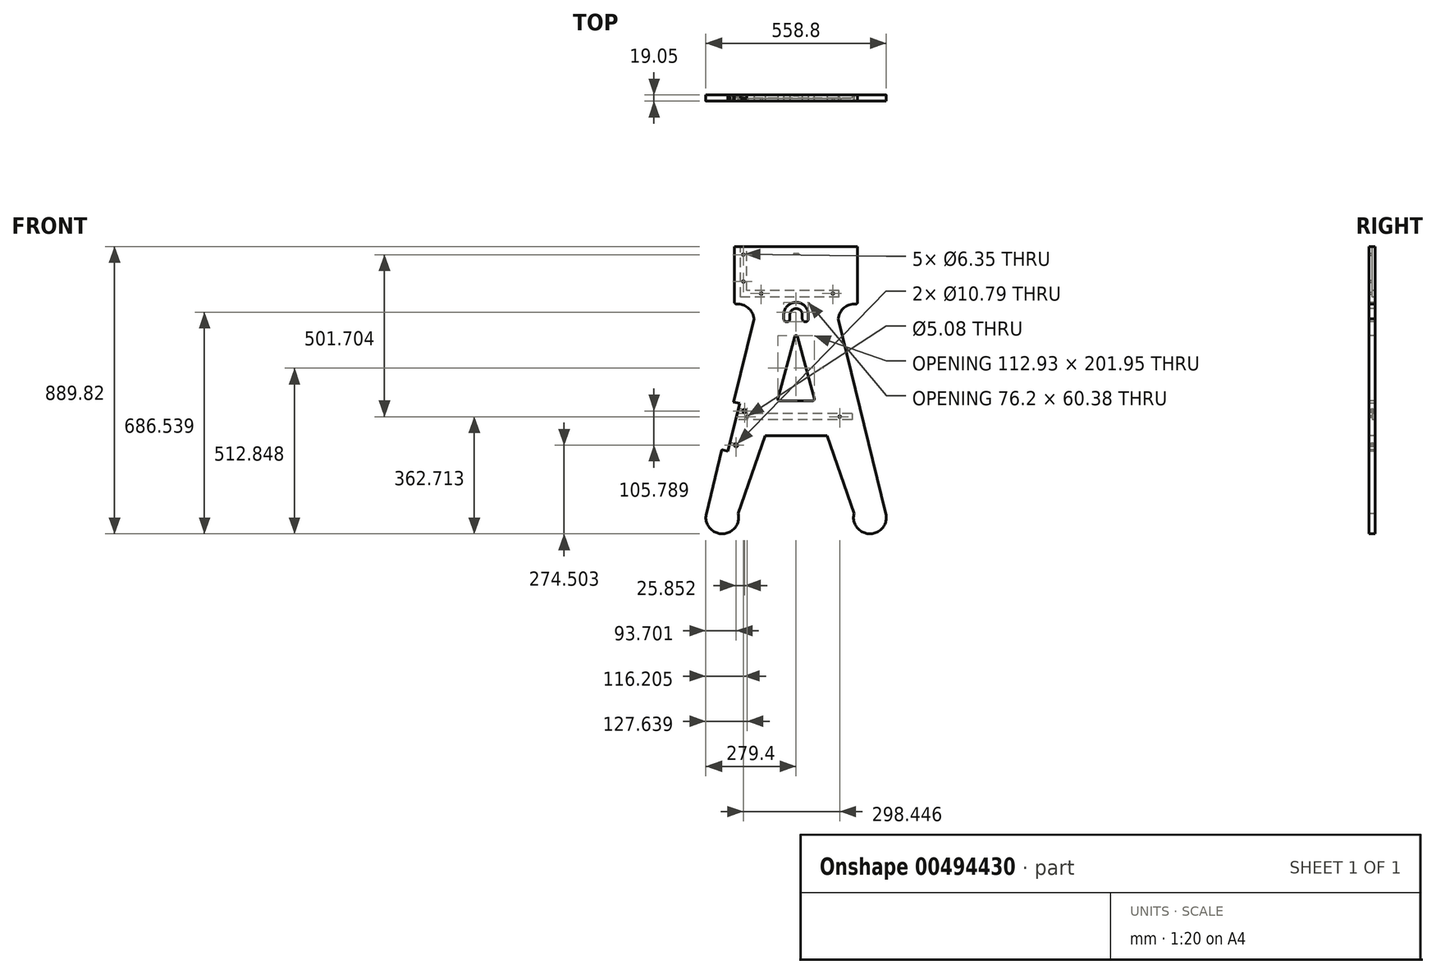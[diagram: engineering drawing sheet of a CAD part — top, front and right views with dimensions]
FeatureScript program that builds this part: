
annotation { "Feature Type Name" : "Feature", "Feature Type Description" : "" }
export const myFeature = defineFeature(function(context is Context, id is Id, definition is map)
    precondition{}
    {
        {
            var Q0;
            Q0=qCreatedBy(makeId("Front.planeOp"),FACE);
            var sketch = newSketch(context, id + "F0", { "sketchPlane" : qUnion([Q0])});
            skLineSegment(sketch, "E0", {"start": v(-190.5, 125.54) * mm, "end": v(-190.5, -53.23) * mm});
            skLineSegment(sketch, "E1", {"start": v(-173.35, -392.04) * mm, "end": v(-173.35, -411.49) * mm});
            skPoint(sketch, "E2.visualSharp", {"position": v(-190.5, -52.26) * mm});
            skLineSegment(sketch, "E3", {"start": v(-152.4, -30.85) * mm, "end": v(-152.4, -11.4) * mm});
            skLineSegment(sketch, "E4", {"start": v(0, -85.65) * mm, "end": v(0, -6.48) * mm, "construction": true});
            skLineSegment(sketch, "E5", {"start": v(-130.6, -98.45) * mm, "end": v(-277.95, -701.42) * mm});
            skArc(sketch, "E6", {"start": v(-277.95, -701.42) * mm, "mid": v(-228.6, -764.28) * mm, "end": v(-179.25, -701.42) * mm});
            skLineSegment(sketch, "E7", {"start": v(0, 125.54) * mm, "end": v(0, -789) * mm, "construction": true});
            skPoint(sketch, "E8", {"position": v(-95.55, -460.12) * mm});
            skPoint(sketch, "E9", {"position": v(0, -135.91) * mm});
            skPoint(sketch, "E10", {"position": v(-58, -352.4) * mm});
            skLineSegment(sketch, "E11", {"start": v(0, -400.38) * mm, "end": v(0, -411.49) * mm});
            skLineSegment(sketch, "E12", {"start": v(-179.25, -701.42) * mm, "end": v(-95.55, -460.12) * mm});
            skLineSegment(sketch, "E13", {"start": v(95.55, -460.12) * mm, "end": v(-95.55, -460.12) * mm});
            skLineSegment(sketch, "E14", {"start": v(0, -135.91) * mm, "end": v(-58, -352.4) * mm});
            skLineSegment(sketch, "E15", {"start": v(-200.12, -382.94) * mm, "end": v(-236.3, -530.98) * mm});
            skLineSegment(sketch, "E16", {"start": v(-193.57, -356.14) * mm, "end": v(-175.06, -360.66) * mm});
            skLineSegment(sketch, "E17", {"start": v(-175.06, -360.66) * mm, "end": v(-211.24, -508.7) * mm});
            skLineSegment(sketch, "E18", {"start": v(-211.24, -508.7) * mm, "end": v(-229.75, -504.18) * mm});
            skPoint(sketch, "E19", {"position": v(-228.6, -764.28) * mm});
            skLineSegment(sketch, "E20", {"start": v(-228.6, -764.28) * mm, "end": v(190.5, -764.28) * mm, "construction": true});
            skLineSegment(sketch, "E21.MirrorCS", {"start": v(-171.45, 124.72) * mm, "end": v(-209.55, 124.72) * mm, "construction": true});
            skLineSegment(sketch, "E22", {"start": v(-190.5, 125.54) * mm, "end": v(-228.6, 125.54) * mm, "construction": true});
            skPoint(sketch, "E23", {"position": v(-173.35, -392.04) * mm});
            skPoint(sketch, "E24", {"position": v(-173.35, -411.49) * mm});
            skLineSegment(sketch, "E25", {"start": v(-173.35, -392.04) * mm, "end": v(173.35, -392.04) * mm});
            skLineSegment(sketch, "E26", {"start": v(173.35, -411.49) * mm, "end": v(-173.35, -411.49) * mm});
            skLineSegment(sketch, "E27", {"start": v(-228.6, 125.54) * mm, "end": v(-228.6, -764.28) * mm, "construction": true});
            skPoint(sketch, "E28", {"position": v(0, 125.54) * mm});
            skPoint(sketch, "E29", {"position": v(0, -11.4) * mm});
            skPoint(sketch, "E30", {"position": v(0, -30.85) * mm});
            skPoint(sketch, "E31", {"position": v(0, -66.6) * mm});
            skPoint(sketch, "E32", {"position": v(0, -46.07) * mm});
            skPoint(sketch, "E33", {"position": v(0, -104.7) * mm});
            skPoint(sketch, "E34", {"position": v(0, -352.4) * mm});
            skPoint(sketch, "E35", {"position": v(0, -460.12) * mm});
            skPoint(sketch, "E36", {"position": v(-19.05, -701.42) * mm});
            skLineSegment(sketch, "E37", {"start": v(0, -460.12) * mm, "end": v(95.55, -460.12) * mm});
            skLineSegment(sketch, "E38", {"start": v(0, -411.49) * mm, "end": v(173.35, -411.49) * mm});
            skLineSegment(sketch, "E39", {"start": v(173.35, -392.04) * mm, "end": v(0, -392.04) * mm});
            skLineSegment(sketch, "E40", {"start": v(-179.25, -701.42) * mm, "end": v(-19.05, -701.42) * mm});
            skLineSegment(sketch, "E41", {"start": v(0, 125.54) * mm, "end": v(-190.5, 125.54) * mm});
            skLineSegment(sketch, "E42", {"start": v(0, -11.4) * mm, "end": v(-152.4, -11.4) * mm});
            skLineSegment(sketch, "E43", {"start": v(-152.4, -30.85) * mm, "end": v(0, -30.85) * mm});
            skLineSegment(sketch, "E44", {"start": v(-58, -352.4) * mm, "end": v(0, -352.4) * mm});
            skLineSegment(sketch, "E45.MirrorCS", {"start": v(0, 125.54) * mm, "end": v(190.5, 125.54) * mm});
            skLineSegment(sketch, "E46.MirrorCS", {"start": v(190.5, 125.54) * mm, "end": v(190.5, -53.23) * mm});
            skLineSegment(sketch, "E47.MirrorCS", {"start": v(0, -11.4) * mm, "end": v(152.4, -11.4) * mm});
            skLineSegment(sketch, "E48.MirrorCS", {"start": v(152.4, -30.85) * mm, "end": v(0, -30.85) * mm});
            skLineSegment(sketch, "E49.MirrorCS", {"start": v(152.4, -30.85) * mm, "end": v(152.4, -11.4) * mm});
            skLineSegment(sketch, "E50.MirrorCS", {"start": v(130.6, -98.45) * mm, "end": v(277.95, -701.42) * mm});
            skLineSegment(sketch, "E51.MirrorCS", {"start": v(0, -135.91) * mm, "end": v(58, -352.4) * mm});
            skLineSegment(sketch, "E52.MirrorCS", {"start": v(58, -352.4) * mm, "end": v(0, -352.4) * mm});
            skLineSegment(sketch, "E53.MirrorCS", {"start": v(173.35, -392.04) * mm, "end": v(173.35, -411.49) * mm});
            skLineSegment(sketch, "E54.MirrorCS", {"start": v(179.25, -701.42) * mm, "end": v(95.55, -460.12) * mm});
            skArc(sketch, "E55.MirrorCS", {"start": v(277.95, -701.42) * mm, "mid": v(228.6, -764.28) * mm, "end": v(179.25, -701.42) * mm});
            skArc(sketch, "E56", {"start": v(-130.6, -98.45) * mm, "mid": v(-150.57, -62.62) * mm, "end": v(-190.5, -53.23) * mm});
            skArc(sketch, "E57.MirrorCS", {"start": v(130.6, -98.45) * mm, "mid": v(150.57, -62.62) * mm, "end": v(190.5, -53.23) * mm});
            skLineSegment(sketch, "E58.top", {"start": v(152.4, 125.54) * mm, "end": v(171.85, 125.54) * mm});
            skLineSegment(sketch, "E59.MirrorCS", {"start": v(-152.4, -30.85) * mm, "end": v(-152.4, 125.54) * mm});
            skLineSegment(sketch, "E60.MirrorCS", {"start": v(-171.85, -30.85) * mm, "end": v(-171.85, 125.54) * mm});
            skLineSegment(sketch, "E61.MirrorCS", {"start": v(-152.4, -30.85) * mm, "end": v(-171.45, -30.85) * mm});
            skLineSegment(sketch, "E62", {"start": v(132.95, -30.85) * mm, "end": v(132.95, -11.4) * mm});
            skLineSegment(sketch, "E63", {"start": v(-173.35, -392.04) * mm, "end": v(-182.73, -392.04) * mm});
            skLineSegment(sketch, "E64", {"start": v(-173.35, -411.49) * mm, "end": v(-187.49, -411.49) * mm});
            skLineSegment(sketch, "E65", {"start": v(0, -85.65) * mm, "end": v(-19.05, -85.65) * mm, "construction": true});
            skLineSegment(sketch, "E66", {"start": v(-19.05, -85.65) * mm, "end": v(-19.05, -98.35) * mm});
            skLineSegment(sketch, "E67", {"start": v(-38.1, -85.73) * mm, "end": v(-38.07, -98.43) * mm});
            skLineSegment(sketch, "E68", {"start": v(-28.65, -83.45) * mm, "end": v(-28.65, -98.43) * mm, "construction": true});
            skCircle(sketch, "E69", {"center": v(-28.65, -98.43) * mm, "radius": 9.53 * mm});
            skLineSegment(sketch, "E70", {"start": v(-19.05, -98.35) * mm, "end": v(-19.13, -98.44) * mm});
            skLineSegment(sketch, "E71", {"start": v(-38.07, -98.43) * mm, "end": v(-38.17, -98.57) * mm});
            skLineSegment(sketch, "E72.MirrorCS", {"start": v(19.05, -85.65) * mm, "end": v(19.05, -98.35) * mm});
            skLineSegment(sketch, "E73.MirrorCS", {"start": v(38.1, -85.73) * mm, "end": v(38.07, -98.43) * mm});
            skCircle(sketch, "E74.MirrorC", {"center": v(28.65, -98.43) * mm, "radius": 9.53 * mm});
            skLineSegment(sketch, "E75.MirrorCS", {"start": v(38.07, -98.43) * mm, "end": v(38.17, -98.57) * mm});
            skLineSegment(sketch, "E76.MirrorCS", {"start": v(19.05, -98.35) * mm, "end": v(19.13, -98.44) * mm});
            skArc(sketch, "E77", {"start": v(19.05, -85.65) * mm, "mid": v(0, -66.6) * mm, "end": v(-19.05, -85.65) * mm});
            skArc(sketch, "E78", {"start": v(38.1, -85.73) * mm, "mid": v(0, -47.55) * mm, "end": v(-38.1, -85.73) * mm});
            skLineSegment(sketch, "E79", {"start": v(-171.45, -30.85) * mm, "end": v(-171.85, -30.85) * mm});
            skSolve(sketch);
        }
        {
            var Q0;
            {var subQ3=sQuery(id+"F0.wireOp",EDGE,"E0");Q0=makeQuery(id+"F0.imprint","IMPRINT",FACE,{"disambiguationData":[TD([[makeQuery(id+"F0.imprint","IMPRINT",EDGE,{"derivedFrom":subQ3}),1.0]])]});}
            var Q1;
            {var subQ0=sQuery(id+"F0.wireOp",EDGE,"QdZ4q6tu-XtS0-hKuG-SYT6-mvfXEwVYjuRs");var subQ1=sQuery(id+"F0.wireOp",EDGE,"5CLiYZQ8-SurR-FD3a-r9Za-pOOhqkRFUcFN");var subQ2=makeQuery(id+"F0.imprint","INTERSECT",VERTEX,{"derivedFrom":[subQ1,subQ0]});Q1=makeQuery(id+"F0.imprint","IMPRINT",FACE,{"disambiguationData":[TD([[makeQuery(id+"F0.imprint","IMPRINT",EDGE,{"disambiguationData":[TD([[subQ2,-1.0]])],"derivedFrom":subQ1}),1.0]])]});}
            var Q2;
            {var subQ0=sQuery(id+"F0.wireOp",EDGE,"QdZ4q6tu-XtS0-hKuG-SYT6-mvfXEwVYjuRs");var subQ1=sQuery(id+"F0.wireOp",EDGE,"yDFHAGDt-Kqkx-1beu-0St6-xb6w35ufjKSX");var subQ2=makeQuery(id+"F0.imprint","INTERSECT",VERTEX,{"disambiguationData":[OD(0.0)],"derivedFrom":[subQ1,subQ0]});Q2=makeQuery(id+"F0.imprint","IMPRINT",FACE,{"disambiguationData":[TD([[makeQuery(id+"F0.imprint","IMPRINT",EDGE,{"disambiguationData":[TD([[subQ2,1.0]])],"derivedFrom":subQ1}),1.0]])]});}
            var Q3;
            {var subQ0=sQuery(id+"F0.wireOp",EDGE,"E49.MirrorCS");Q3=makeQuery(id+"F0.imprint","IMPRINT",FACE,{"disambiguationData":[TD([[makeQuery(id+"F0.imprint","IMPRINT",EDGE,{"derivedFrom":subQ0}),1.0]])]});}
            extrude(context, id + "F1", {"entities" : qUnion([Q0, Q1, Q2, Q3]), "depth" : 19.05 * mm, "offsetDistance" : 25.4 * mm});
        }
        {
            var Q0;
            {var subQ0=sQuery(id+"F0.wireOp",EDGE,"TeCzVH9V-o8Gh-6CSs-Ju1C-ZN7UWPDbQMcw");Q0=makeQuery(id+"F0.imprint","IMPRINT",FACE,{"disambiguationData":[TD([[makeQuery(id+"F0.imprint","IMPRINT",EDGE,{"derivedFrom":subQ0}),1.0]])]});}
            var Q1;
            Q1=makeQuery(id+"F0.imprint","IMPRINT",FACE,{"disambiguationData":[TD([[makeQuery(id+"F0.imprint","IMPRINT",EDGE,{"derivedFrom":sQuery(id+"F0.wireOp",EDGE,"3cQowQxt-8lGC-4pJi-Gm52-UmAgLV0NdpkX")}),1.0]])]});
            var Q2;
            Q2=makeQuery(id+"F0.imprint","IMPRINT",FACE,{"disambiguationData":[TD([[makeQuery(id+"F0.imprint","IMPRINT",EDGE,{"derivedFrom":sQuery(id+"F0.wireOp",EDGE,"E11")}),1.0]])]});
            var Q3;
            Q3=makeQuery(id+"F0.imprint","IMPRINT",FACE,{"disambiguationData":[TD([[makeQuery(id+"F0.imprint","IMPRINT",EDGE,{"derivedFrom":sQuery(id+"F0.wireOp",EDGE,"E1")}),1.0]])]});
            var Q4;
            Q4=makeQuery(id+"F0.imprint","IMPRINT",FACE,{"disambiguationData":[TD([[makeQuery(id+"F0.imprint","IMPRINT",EDGE,{"derivedFrom":sQuery(id+"F0.wireOp",EDGE,"E3")}),-1.0]])]});
            var Q5;
            {var subQ3=sQuery(id+"F0.wireOp",EDGE,"KYvBSgZk-RGwW-1GSw-zPPc-KfTGoLaRr0VA");Q5=makeQuery(id+"F0.imprint","IMPRINT",FACE,{"disambiguationData":[TD([[makeQuery(id+"F0.imprint","IMPRINT",EDGE,{"derivedFrom":subQ3}),1.0]])]});}
            var Q6;
            {var subQ3=sQuery(id+"F0.wireOp",EDGE,"E58.bottom");Q6=makeQuery(id+"F0.imprint","IMPRINT",FACE,{"disambiguationData":[TD([[makeQuery(id+"F0.imprint","IMPRINT",EDGE,{"derivedFrom":subQ3}),1.0]])]});}
            var Q7;
            {var subQ1=sQuery(id+"F0.wireOp",EDGE,"E42");Q7=makeQuery(id+"F0.imprint","IMPRINT",FACE,{"disambiguationData":[TD([[makeQuery(id+"F0.imprint","IMPRINT",EDGE,{"derivedFrom":subQ1}),1.0]])]});}
            var Q8;
            {var subQ0=sQuery(id+"F0.wireOp",EDGE,"E60.MirrorCS");Q8=makeQuery(id+"F0.imprint","IMPRINT",FACE,{"disambiguationData":[TD([[makeQuery(id+"F0.imprint","IMPRINT",EDGE,{"derivedFrom":subQ0}),-1.0]])]});}
            var Q9;
            Q9=makeQuery(id+"F0.imprint","IMPRINT",FACE,{"disambiguationData":[TD([[makeQuery(id+"F0.imprint","IMPRINT",EDGE,{"derivedFrom":sQuery(id+"F0.wireOp",EDGE,"E1")}),-1.0]])]});
            extrude(context, id + "F2", {"entities" : qUnion([Q0, Q1, Q2, Q3, Q4, Q5, Q6, Q7, Q8, Q9]), "operationType" : NewBodyOperationType.ADD, "depth" : 9.52 * mm, "offsetDistance" : 25.4 * mm});
        }
        {
            var Q0;
            Q0=makeQuery(id+"F1.opExtrude","SWEPT_EDGE",EDGE,{"disambiguationData":[OSD([sQuery(id+"F0.wireOp",EDGE,"7N1KOc0i-WMFj-BSh4-6628-kfTSEV4ZKCQJ"),sQuery(id+"F0.wireOp",EDGE,"E5")])]});
            var Q1;
            Q1=makeQuery(id+"F1.opExtrude","SWEPT_EDGE",EDGE,{"disambiguationData":[OSD([sQuery(id+"F0.wireOp",EDGE,"E6"),sQuery(id+"F0.wireOp",EDGE,"eo0T7eUB-C7nI-ALEf-IgIR-F7AO5eFVOBVV"),sQuery(id+"F0.wireOp",EDGE,"E12")])]});
            fillet(context, id + "F3", {"entities" : qUnion([Q0, Q1]), "radius" : 0.38 * mm, "tangentPropagation" : true, "defaultsChanged" : false, "vertexSettings" : [], "allowEdgeOverflow" : false});
        }
        {
            var Q0;
            {var subQ0=sQuery(id+"F0.wireOp",EDGE,"E16");Q0=makeQuery(id+"F0.imprint","IMPRINT",FACE,{"disambiguationData":[TD([[makeQuery(id+"F0.imprint","IMPRINT",EDGE,{"derivedFrom":subQ0}),-1.0]])]});}
            var sketch = newSketch(context, id + "F4", { "sketchPlane" : qUnion([Q0])});
            skCircle(sketch, "E80", {"center": v(-159.85, -383.99) * mm, "radius": 5.4 * mm});
            skCircle(sketch, "E81", {"center": v(-185.7, -489.78) * mm, "radius": 5.4 * mm});
            skCircle(sketch, "E82", {"center": v(-107.95, -20.12) * mm, "radius": 3.18 * mm});
            skCircle(sketch, "E83", {"center": v(-151.76, -401.57) * mm, "radius": 2.54 * mm});
            skCircle(sketch, "E84.MirrorC", {"center": v(135.25, -401.57) * mm, "radius": 3.18 * mm});
            skCircle(sketch, "E85.MirrorC", {"center": v(-163.2, 100.14) * mm, "radius": 3.18 * mm});
            skCircle(sketch, "E86.MirrorC", {"center": v(-163.2, 16.77) * mm, "radius": 3.18 * mm});
            skCircle(sketch, "E87", {"center": v(113.93, -20.12) * mm, "radius": 3.18 * mm});
            skSolve(sketch);
        }
        {
            var Q0;
            Q0=qSketchRegion(id+"F4",true);
            extrude(context, id + "F5", {"entities" : qUnion([Q0]), "operationType" : NewBodyOperationType.REMOVE, "depth" : 25.4 * mm, "offsetDistance" : 25.4 * mm});
        }
        {
            var Q0;
            Q0=makeQuery(id+"F1.opExtrude","SWEPT_EDGE",EDGE,{"disambiguationData":[OSD([sQuery(id+"F0.wireOp",EDGE,"E0"),sQuery(id+"F0.wireOp",EDGE,"E56")])]});
            var Q1;
            Q1=makeQuery(id+"F1.opExtrude","SWEPT_EDGE",EDGE,{"disambiguationData":[OSD([sQuery(id+"F0.wireOp",EDGE,"E46.MirrorCS"),sQuery(id+"F0.wireOp",EDGE,"E57.MirrorCS")])]});
            fillet(context, id + "F6", {"entities" : qUnion([Q0, Q1]), "radius" : 5.08 * mm, "tangentPropagation" : true, "allowEdgeOverflow" : false});
        }
        {
            var Q0;
            Q0=makeQuery(id+"F1.opExtrude","SWEPT_EDGE",EDGE,{"disambiguationData":[OSD([sQuery(id+"F0.wireOp",EDGE,"E14"),sQuery(id+"F0.wireOp",EDGE,"E51.MirrorCS")])]});
            var Q1;
            Q1=makeQuery(id+"F1.opExtrude","SWEPT_EDGE",EDGE,{"disambiguationData":[OSD([sQuery(id+"F0.wireOp",EDGE,"E14"),sQuery(id+"F0.wireOp",EDGE,"E44")])]});
            var Q2;
            Q2=makeQuery(id+"F1.opExtrude","SWEPT_EDGE",EDGE,{"disambiguationData":[OSD([sQuery(id+"F0.wireOp",EDGE,"E51.MirrorCS"),sQuery(id+"F0.wireOp",EDGE,"E52.MirrorCS")])]});
            fillet(context, id + "F7", {"entities" : qUnion([Q0, Q1, Q2]), "radius" : 5.08 * mm, "tangentPropagation" : true, "allowEdgeOverflow" : false});
        }
        {
            var Q0;
            Q0=makeQuery(id+"F1.opExtrude","SWEPT_BODY",BODY,{"disambiguationData":[OSD([sQuery(id+"F0.wireOp",EDGE,"E0"),sQuery(id+"F0.wireOp",EDGE,"E1"),sQuery(id+"F0.wireOp",EDGE,"E3"),sQuery(id+"F0.wireOp",EDGE,"5CLiYZQ8-SurR-FD3a-r9Za-pOOhqkRFUcFN"),sQuery(id+"F0.wireOp",EDGE,"yDFHAGDt-Kqkx-1beu-0St6-xb6w35ufjKSX"),sQuery(id+"F0.wireOp",EDGE,"QdZ4q6tu-XtS0-hKuG-SYT6-mvfXEwVYjuRs"),sQuery(id+"F0.wireOp",EDGE,"a26f25c3-d710-456f-8808-1fd3088ace820.MirrorCS"),sQuery(id+"F0.wireOp",EDGE,"E5"),sQuery(id+"F0.wireOp",EDGE,"E6"),sQuery(id+"F0.wireOp",EDGE,"E12"),sQuery(id+"F0.wireOp",EDGE,"E13"),sQuery(id+"F0.wireOp",EDGE,"E15"),sQuery(id+"F0.wireOp",EDGE,"E16"),sQuery(id+"F0.wireOp",EDGE,"E17"),sQuery(id+"F0.wireOp",EDGE,"E18"),sQuery(id+"F0.wireOp",EDGE,"E25"),sQuery(id+"F0.wireOp",EDGE,"E26"),sQuery(id+"F0.wireOp",EDGE,"E37"),sQuery(id+"F0.wireOp",EDGE,"E38"),sQuery(id+"F0.wireOp",EDGE,"E39"),sQuery(id+"F0.wireOp",EDGE,"E41"),sQuery(id+"F0.wireOp",EDGE,"E42"),sQuery(id+"F0.wireOp",EDGE,"E43"),sQuery(id+"F0.wireOp",EDGE,"E14"),sQuery(id+"F0.wireOp",EDGE,"E44"),sQuery(id+"F0.wireOp",EDGE,"E45.MirrorCS"),sQuery(id+"F0.wireOp",EDGE,"E46.MirrorCS"),sQuery(id+"F0.wireOp",EDGE,"E47.MirrorCS"),sQuery(id+"F0.wireOp",EDGE,"E48.MirrorCS"),sQuery(id+"F0.wireOp",EDGE,"E50.MirrorCS"),sQuery(id+"F0.wireOp",EDGE,"E51.MirrorCS"),sQuery(id+"F0.wireOp",EDGE,"E52.MirrorCS"),sQuery(id+"F0.wireOp",EDGE,"E53.MirrorCS"),sQuery(id+"F0.wireOp",EDGE,"E54.MirrorCS"),sQuery(id+"F0.wireOp",EDGE,"E55.MirrorCS"),sQuery(id+"F0.wireOp",EDGE,"E56"),sQuery(id+"F0.wireOp",EDGE,"E57.MirrorCS"),sQuery(id+"F0.wireOp",EDGE,"E58.bottom"),sQuery(id+"F0.wireOp",EDGE,"E58.left"),sQuery(id+"F0.wireOp",EDGE,"E58.right")])]});
            var Q1;
            Q1=makeQuery(id+"F1.opExtrude","CAP_FACE",FACE,{"disambiguationData":[OSD([sQuery(id+"F0.wireOp",EDGE,"E0"),sQuery(id+"F0.wireOp",EDGE,"E1"),sQuery(id+"F0.wireOp",EDGE,"E3"),sQuery(id+"F0.wireOp",EDGE,"5CLiYZQ8-SurR-FD3a-r9Za-pOOhqkRFUcFN"),sQuery(id+"F0.wireOp",EDGE,"yDFHAGDt-Kqkx-1beu-0St6-xb6w35ufjKSX"),sQuery(id+"F0.wireOp",EDGE,"QdZ4q6tu-XtS0-hKuG-SYT6-mvfXEwVYjuRs"),sQuery(id+"F0.wireOp",EDGE,"a26f25c3-d710-456f-8808-1fd3088ace820.MirrorCS"),sQuery(id+"F0.wireOp",EDGE,"E5"),sQuery(id+"F0.wireOp",EDGE,"E6"),sQuery(id+"F0.wireOp",EDGE,"E12"),sQuery(id+"F0.wireOp",EDGE,"E13"),sQuery(id+"F0.wireOp",EDGE,"E15"),sQuery(id+"F0.wireOp",EDGE,"E16"),sQuery(id+"F0.wireOp",EDGE,"E17"),sQuery(id+"F0.wireOp",EDGE,"E18"),sQuery(id+"F0.wireOp",EDGE,"E25"),sQuery(id+"F0.wireOp",EDGE,"E26"),sQuery(id+"F0.wireOp",EDGE,"E37"),sQuery(id+"F0.wireOp",EDGE,"E38"),sQuery(id+"F0.wireOp",EDGE,"E39"),sQuery(id+"F0.wireOp",EDGE,"E41"),sQuery(id+"F0.wireOp",EDGE,"E42"),sQuery(id+"F0.wireOp",EDGE,"E43"),sQuery(id+"F0.wireOp",EDGE,"E14"),sQuery(id+"F0.wireOp",EDGE,"E44"),sQuery(id+"F0.wireOp",EDGE,"E45.MirrorCS"),sQuery(id+"F0.wireOp",EDGE,"E46.MirrorCS"),sQuery(id+"F0.wireOp",EDGE,"E47.MirrorCS"),sQuery(id+"F0.wireOp",EDGE,"E48.MirrorCS"),sQuery(id+"F0.wireOp",EDGE,"E50.MirrorCS"),sQuery(id+"F0.wireOp",EDGE,"E51.MirrorCS"),sQuery(id+"F0.wireOp",EDGE,"E52.MirrorCS"),sQuery(id+"F0.wireOp",EDGE,"E53.MirrorCS"),sQuery(id+"F0.wireOp",EDGE,"E54.MirrorCS"),sQuery(id+"F0.wireOp",EDGE,"E55.MirrorCS"),sQuery(id+"F0.wireOp",EDGE,"E56"),sQuery(id+"F0.wireOp",EDGE,"E57.MirrorCS"),sQuery(id+"F0.wireOp",EDGE,"E58.bottom"),sQuery(id+"F0.wireOp",EDGE,"E58.left"),sQuery(id+"F0.wireOp",EDGE,"E58.right")])],"isStart":false});
            mirror(context, id + "F8", {"entities" : qUnion([Q0]), "mirrorPlane" : qUnion([Q1])});
        }
        {
            var Q0;
            Q0=makeQuery(id+"F1.opExtrude","SWEPT_BODY",BODY,{"disambiguationData":[OSD([sQuery(id+"F0.wireOp",EDGE,"E0"),sQuery(id+"F0.wireOp",EDGE,"E1"),sQuery(id+"F0.wireOp",EDGE,"E3"),sQuery(id+"F0.wireOp",EDGE,"5CLiYZQ8-SurR-FD3a-r9Za-pOOhqkRFUcFN"),sQuery(id+"F0.wireOp",EDGE,"yDFHAGDt-Kqkx-1beu-0St6-xb6w35ufjKSX"),sQuery(id+"F0.wireOp",EDGE,"QdZ4q6tu-XtS0-hKuG-SYT6-mvfXEwVYjuRs"),sQuery(id+"F0.wireOp",EDGE,"a26f25c3-d710-456f-8808-1fd3088ace820.MirrorCS"),sQuery(id+"F0.wireOp",EDGE,"E5"),sQuery(id+"F0.wireOp",EDGE,"E6"),sQuery(id+"F0.wireOp",EDGE,"E12"),sQuery(id+"F0.wireOp",EDGE,"E13"),sQuery(id+"F0.wireOp",EDGE,"E15"),sQuery(id+"F0.wireOp",EDGE,"E16"),sQuery(id+"F0.wireOp",EDGE,"E17"),sQuery(id+"F0.wireOp",EDGE,"E18"),sQuery(id+"F0.wireOp",EDGE,"E25"),sQuery(id+"F0.wireOp",EDGE,"E26"),sQuery(id+"F0.wireOp",EDGE,"E37"),sQuery(id+"F0.wireOp",EDGE,"E38"),sQuery(id+"F0.wireOp",EDGE,"E39"),sQuery(id+"F0.wireOp",EDGE,"E41"),sQuery(id+"F0.wireOp",EDGE,"E42"),sQuery(id+"F0.wireOp",EDGE,"E43"),sQuery(id+"F0.wireOp",EDGE,"E14"),sQuery(id+"F0.wireOp",EDGE,"E44"),sQuery(id+"F0.wireOp",EDGE,"E45.MirrorCS"),sQuery(id+"F0.wireOp",EDGE,"E46.MirrorCS"),sQuery(id+"F0.wireOp",EDGE,"E47.MirrorCS"),sQuery(id+"F0.wireOp",EDGE,"E48.MirrorCS"),sQuery(id+"F0.wireOp",EDGE,"E50.MirrorCS"),sQuery(id+"F0.wireOp",EDGE,"E51.MirrorCS"),sQuery(id+"F0.wireOp",EDGE,"E52.MirrorCS"),sQuery(id+"F0.wireOp",EDGE,"E53.MirrorCS"),sQuery(id+"F0.wireOp",EDGE,"E54.MirrorCS"),sQuery(id+"F0.wireOp",EDGE,"E55.MirrorCS"),sQuery(id+"F0.wireOp",EDGE,"E56"),sQuery(id+"F0.wireOp",EDGE,"E57.MirrorCS"),sQuery(id+"F0.wireOp",EDGE,"E58.bottom"),sQuery(id+"F0.wireOp",EDGE,"E58.left"),sQuery(id+"F0.wireOp",EDGE,"E58.right")])]});
            deleteBodies(context, id + "F9", {"entities" : qUnion([Q0])});
        }
        {
            var Q0;
            {var subQ0=sQuery(id+"F0.wireOp",EDGE,"E62");var subQ1=sQuery(id+"F0.wireOp",EDGE,"E61.MirrorCS");var subQ2=sQuery(id+"F0.wireOp",EDGE,"E60.MirrorCS");var subQ3=sQuery(id+"F0.wireOp",EDGE,"E59.MirrorCS");var subQ4=sQuery(id+"F0.wireOp",EDGE,"E48.MirrorCS");var subQ5=sQuery(id+"F0.wireOp",EDGE,"E47.MirrorCS");var subQ6=sQuery(id+"F0.wireOp",EDGE,"E43");var subQ7=sQuery(id+"F0.wireOp",EDGE,"E42");var subQ8=sQuery(id+"F0.wireOp",EDGE,"E41");var subQ9=sQuery(id+"F0.wireOp",EDGE,"E64");var subQ10=sQuery(id+"F0.wireOp",EDGE,"E63");var subQ11=sQuery(id+"F0.wireOp",EDGE,"E53.MirrorCS");var subQ12=sQuery(id+"F0.wireOp",EDGE,"E39");var subQ13=sQuery(id+"F0.wireOp",EDGE,"E38");var subQ14=sQuery(id+"F0.wireOp",EDGE,"E26");var subQ15=sQuery(id+"F0.wireOp",EDGE,"E25");var subQ16=sQuery(id+"F0.wireOp",EDGE,"E17");Q0=makeQuery(id+"F8.opPattern","COPY",FACE,{"derivedFrom":makeQuery(id+"F2.boolean.opBoolean","MERGE",FACE,{"derivedFrom":[makeQuery(id+"F1.opExtrude","CAP_FACE",FACE,{"disambiguationData":[OSD([sQuery(id+"F0.wireOp",EDGE,"E0"),sQuery(id+"F0.wireOp",EDGE,"E5"),sQuery(id+"F0.wireOp",EDGE,"E6"),sQuery(id+"F0.wireOp",EDGE,"E12"),sQuery(id+"F0.wireOp",EDGE,"E13"),sQuery(id+"F0.wireOp",EDGE,"E15"),sQuery(id+"F0.wireOp",EDGE,"E16"),subQ16,sQuery(id+"F0.wireOp",EDGE,"E18"),subQ15,subQ14,sQuery(id+"F0.wireOp",EDGE,"E37"),subQ13,subQ12,subQ8,subQ7,subQ6,sQuery(id+"F0.wireOp",EDGE,"E14"),sQuery(id+"F0.wireOp",EDGE,"E44"),sQuery(id+"F0.wireOp",EDGE,"E45.MirrorCS"),sQuery(id+"F0.wireOp",EDGE,"E46.MirrorCS"),subQ5,subQ4,sQuery(id+"F0.wireOp",EDGE,"E50.MirrorCS"),sQuery(id+"F0.wireOp",EDGE,"E51.MirrorCS"),sQuery(id+"F0.wireOp",EDGE,"E52.MirrorCS"),subQ11,sQuery(id+"F0.wireOp",EDGE,"E54.MirrorCS"),sQuery(id+"F0.wireOp",EDGE,"E55.MirrorCS"),sQuery(id+"F0.wireOp",EDGE,"E56"),sQuery(id+"F0.wireOp",EDGE,"E57.MirrorCS"),sQuery(id+"F0.wireOp",EDGE,"E58.top"),subQ3,subQ2,subQ1,subQ0,subQ10,subQ9,sQuery(id+"F0.wireOp",EDGE,"E66"),sQuery(id+"F0.wireOp",EDGE,"E67"),sQuery(id+"F0.wireOp",EDGE,"E69"),sQuery(id+"F0.wireOp",EDGE,"E70"),sQuery(id+"F0.wireOp",EDGE,"E72.MirrorCS"),sQuery(id+"F0.wireOp",EDGE,"E73.MirrorCS"),sQuery(id+"F0.wireOp",EDGE,"E74.MirrorC"),sQuery(id+"F0.wireOp",EDGE,"E76.MirrorCS"),sQuery(id+"F0.wireOp",EDGE,"E77"),sQuery(id+"F0.wireOp",EDGE,"E78")])],"isStart":true}),makeQuery(id+"F2.opExtrude","CAP_FACE",FACE,{"disambiguationData":[OSD([subQ16,subQ15,subQ14,subQ13,subQ12,subQ11,subQ10,subQ9])],"isStart":true}),makeQuery(id+"F2.opExtrude","CAP_FACE",FACE,{"disambiguationData":[OSD([subQ8,subQ7,subQ6,subQ5,subQ4,subQ3,subQ2,subQ1,subQ0])],"isStart":true})]}),"instanceName":"1"});}
            var sketch = newSketch(context, id + "F10", { "sketchPlane" : qUnion([Q0])});
            skLineSegment(sketch, "E88", {"start": v(-159.85, -383.99) * mm, "end": v(-179.59, -379.16) * mm, "construction": true});
            skLineSegment(sketch, "E89", {"start": v(-185.7, -489.78) * mm, "end": v(-205.44, -484.95) * mm, "construction": true});
            skSolve(sketch);
        }
        {
            var Q0;
            {var subQ0=sQuery(id+"F0.wireOp",EDGE,"E17");Q0=makeQuery(id+"F8.opPattern","COPY",FACE,{"derivedFrom":makeQuery(id+"F2.boolean.opBoolean","MERGE",FACE,{"derivedFrom":[makeQuery(id+"F1.opExtrude","SWEPT_FACE",FACE,{"disambiguationData":[OSD([subQ0]),TDD([makeQuery(id+"F0.imprint","IMPRINT",EDGE,{"disambiguationData":[TD([[makeQuery(id+"F0.imprint","INTERSECT",VERTEX,{"derivedFrom":[sQuery(id+"F0.wireOp",EDGE,"E16"),subQ0]}),-1.0]])],"derivedFrom":subQ0})])]}),makeQuery(id+"F1.opExtrude","SWEPT_FACE",FACE,{"disambiguationData":[OSD([subQ0]),TDD([makeQuery(id+"F0.imprint","IMPRINT",EDGE,{"disambiguationData":[TD([[makeQuery(id+"F0.imprint","INTERSECT",VERTEX,{"derivedFrom":[subQ0,sQuery(id+"F0.wireOp",EDGE,"E18")]}),1.0]])],"derivedFrom":subQ0})])]}),makeQuery(id+"F2.opExtrude","SWEPT_FACE",FACE,{"disambiguationData":[OSD([subQ0])]})]}),"instanceName":"1"});}
            var sketch = newSketch(context, id + "F11", { "sketchPlane" : qUnion([Q0])});
            skPoint(sketch, "E90.0", {"position": v(38.1, -410.96) * mm});
            skPoint(sketch, "E91.0", {"position": v(38.1, -519.86) * mm});
            skLineSegment(sketch, "E92", {"start": v(38.1, -410.96) * mm, "end": v(19.05, -410.96) * mm, "construction": true});
            skLineSegment(sketch, "E93", {"start": v(38.1, -519.86) * mm, "end": v(19.05, -519.86) * mm, "construction": true});
            skPoint(sketch, "E94", {"position": v(28.58, -410.96) * mm});
            skPoint(sketch, "E95", {"position": v(28.58, -519.86) * mm});
            skCircle(sketch, "E96", {"center": v(28.58, -519.86) * mm, "radius": 3.18 * mm});
            skCircle(sketch, "E97", {"center": v(28.58, -410.96) * mm, "radius": 3.17 * mm});
            skSolve(sketch);
        }
        {
            var Q0;
            Q0 = qSketchRegion(id + "F11", true);
            extrude(context, id + "F12", {"entities" : qUnion([Q0]), "operationType" : NewBodyOperationType.REMOVE, "endBound" : BoundingType.UP_TO_NEXT, "oppositeDirection" : true, "depth" : 25.4 * mm, "offsetDistance" : 25.4 * mm});
        }
        {
            var Q0;
            {var subQ25=sQuery(id+"F0.wireOp",EDGE,"E0");Q0=makeQuery(id+"F0.imprint","IMPRINT",FACE,{"disambiguationData":[TD([[makeQuery(id+"F0.imprint","IMPRINT",EDGE,{"derivedFrom":subQ25}),1.0]])]});}
            var sketch = newSketch(context, id + "F13", { "sketchPlane" : qUnion([Q0])});
            skLineSegment(sketch, "E98.0", {"start": v(0, 125.54) * mm, "end": v(0, -789) * mm, "construction": true});
            skPoint(sketch, "E99", {"position": v(0, 103.31) * mm});
            skLineSegment(sketch, "E100.bottom", {"start": v(0, 103.31) * mm, "end": v(-8.06, 103.31) * mm});
            skLineSegment(sketch, "E100.top", {"start": v(0, 101.28) * mm, "end": v(-8.06, 101.28) * mm});
            skLineSegment(sketch, "E100.left", {"start": v(0, 103.31) * mm, "end": v(0, 101.28) * mm});
            skLineSegment(sketch, "E100.right", {"start": v(-8.06, 103.31) * mm, "end": v(-8.06, 101.28) * mm});
            skLineSegment(sketch, "E101.MirrorCS", {"start": v(0, 103.31) * mm, "end": v(8.06, 103.31) * mm});
            skLineSegment(sketch, "E102.MirrorCS", {"start": v(8.06, 103.31) * mm, "end": v(8.06, 101.28) * mm});
            skLineSegment(sketch, "E103.MirrorCS", {"start": v(0, 101.28) * mm, "end": v(8.06, 101.28) * mm});
            skSolve(sketch);
        }
        {
            var Q0;
            Q0 = qSketchRegion(id + "F13", true);
            extrude(context, id + "F14", {"entities" : qUnion([Q0]), "operationType" : NewBodyOperationType.REMOVE, "depth" : 22.22 * mm, "offsetDistance" : 25.4 * mm});
        }
    });
